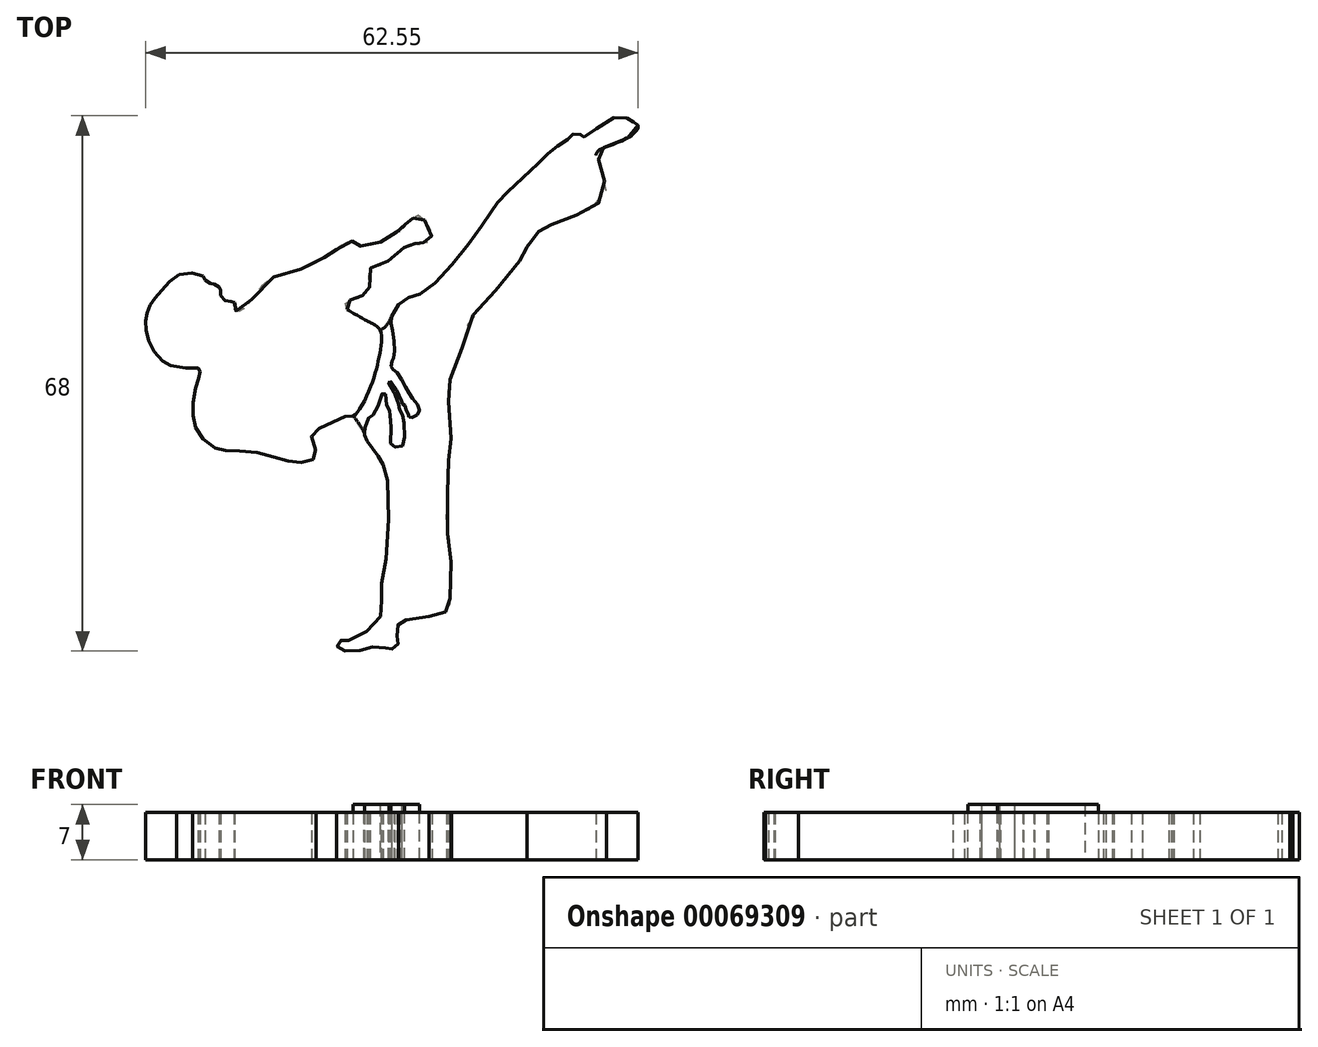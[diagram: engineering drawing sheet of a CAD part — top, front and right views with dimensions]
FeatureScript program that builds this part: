
annotation { "Feature Type Name" : "Feature", "Feature Type Description" : "" }
export const myFeature = defineFeature(function(context is Context, id is Id, definition is map)
    precondition{}
    {
        {
            var Q0;
            Q0=qCreatedBy(makeId("Top.planeOp"),FACE);
            var sketch = newSketch(context, id + "F0", { "sketchPlane" : qUnion([Q0])});
            skFitSpline(sketch, "E0", {"points": [v(-51.75, 44.73) * mm, v(-51.95, 44.9) * mm, v(-52.69, 44.87) * mm, v(-53.47, 45.56) * mm, v(-53.55, 46.35) * mm, v(-53.7, 46.52) * mm, v(-53.72, 46.74) * mm, v(-54.43, 47.11) * mm, v(-54.6, 47.11) * mm, v(-55.44, 47.53) * mm, v(-55.52, 47.92) * mm, v(-58.15, 48.5) * mm, v(-60.84, 46.52) * mm, v(-62.26, 44.78) * mm, v(-62.91, 43.3) * mm, v(-63.01, 41.6) * mm, v(-62.19, 38.9) * mm, v(-60.02, 36.77) * mm, v(-59.1, 36.6) * mm], "startDerivative": vector(-5.65, 8.4) * mm, "endDerivative": vector(13.6, -5.83) * mm});
            skFitSpline(sketch, "E1", {"points": [v(-59.1, 36.6) * mm, v(-58.93, 36.45) * mm, v(-56.37, 36.43) * mm, v(-56.37, 36.3) * mm, v(-56.18, 36.2) * mm, v(-56.26, 35.4) * mm, v(-56.34, 34.96) * mm, v(-56.97, 32.75) * mm, v(-56.97, 30.15) * mm, v(-56.33, 28.15) * mm, v(-53.97, 26.16) * mm, v(-52.28, 25.94) * mm, v(-48.26, 25.57) * mm, v(-44.9, 24.58) * mm, v(-42.47, 24.58) * mm, v(-41.39, 25.43) * mm, v(-41.98, 27.9) * mm, v(-40.1, 29.11) * mm, v(-37.6, 30.32) * mm, v(-36.68, 30.34) * mm, v(-34.38, 34.29) * mm, v(-33.24, 38.67) * mm, v(-33.27, 41.23) * mm, v(-34.84, 42.37) * mm, v(-37.44, 43.89) * mm], "startDerivative": vector(3.1, -12.93) * mm, "endDerivative": vector(-51.13, 31.47) * mm});
            skFitSpline(sketch, "E2", {"points": [v(-37.44, 43.89) * mm, v(-37.67, 44.62) * mm, v(-36.78, 45.13) * mm, v(-35.75, 45.43) * mm, v(-35.16, 46) * mm, v(-34.62, 46.46) * mm, v(-34.62, 49) * mm, v(-33.44, 49.34) * mm, v(-30.65, 51.38) * mm, v(-29.88, 51.98) * mm, v(-29.12, 52.24) * mm, v(-28.12, 52.22) * mm, v(-27.96, 52.4) * mm, v(-27.47, 52.36) * mm, v(-26.84, 52.87) * mm, v(-26.75, 53.72) * mm, v(-28.1, 55.68) * mm, v(-28.84, 55.7) * mm, v(-29.42, 55.05) * mm, v(-29.7, 55) * mm, v(-30.7, 53.95) * mm, v(-31.07, 53.82) * mm, v(-31.57, 53.33) * mm, v(-34.55, 52.02) * mm, v(-36.05, 52.02) * mm, v(-36.45, 52.4) * mm, v(-37.2, 52.5) * mm, v(-38.92, 51.4) * mm, v(-39.89, 50.8) * mm, v(-42.93, 49.1) * mm, v(-47.62, 47.46) * mm, v(-51.02, 43.62) * mm, v(-51.75, 43.89) * mm, v(-51.75, 44.36) * mm, v(-51.75, 44.73) * mm], "startDerivative": vector(-19.72, 33.34) * mm, "endDerivative": vector(-1.61, 21.78) * mm});
            skFitSpline(sketch, "E3", {"points": [v(-0.5, 67.29) * mm, v(-0.95, 67.65) * mm, v(-1.34, 67.68) * mm, v(-2.74, 68.47) * mm, v(-7.15, 65.88) * mm, v(-7.63, 65.81) * mm, v(-7.81, 66.14) * mm, v(-8.73, 66.17) * mm, v(-9.37, 65.51) * mm, v(-11.24, 64.27) * mm, v(-13.23, 62.38) * mm, v(-17.7, 58.2) * mm, v(-19, 56.5) * mm, v(-22.44, 51.68) * mm, v(-28.21, 45.8) * mm, v(-30.08, 45.22) * mm, v(-31.8, 42.95) * mm, v(-31.64, 41.03) * mm, v(-31.52, 37.76) * mm, v(-31.73, 37.35) * mm, v(-31.8, 36.44) * mm, v(-31.33, 36.1) * mm, v(-30.08, 34.08) * mm, v(-29.16, 32.6) * mm, v(-28.26, 31.1) * mm, v(-28.89, 30.26) * mm, v(-29.51, 30.14) * mm, v(-29.66, 30.5) * mm, v(-29.97, 31) * mm, v(-30.15, 31.7) * mm, v(-30.44, 31.9) * mm, v(-30.55, 32.26) * mm], "startDerivative": vector(-22.63, 25.11) * mm, "endDerivative": vector(0.32, 27.82) * mm});
            skFitSpline(sketch, "E4", {"points": [v(-30.55, 32.26) * mm, v(-31.41, 34.1) * mm, v(-32.04, 34.78) * mm, v(-32.22, 34.7) * mm, v(-31.83, 34.04) * mm, v(-30.88, 31.76) * mm, v(-30.8, 31.52) * mm, v(-30.76, 30.88) * mm, v(-30.37, 30.4) * mm, v(-30.24, 29.22) * mm, v(-30.24, 26.75) * mm, v(-30.72, 26.45) * mm, v(-31.65, 26.42) * mm, v(-31.94, 26.9) * mm, v(-31.91, 30.32) * mm, v(-32.12, 30.44) * mm, v(-32.1, 31.06) * mm, v(-32.4, 31.45) * mm, v(-32.58, 33.04) * mm, v(-32.87, 33.42) * mm, v(-33.4, 31.9) * mm, v(-34.21, 30.46) * mm, v(-34.5, 30.43) * mm, v(-35.09, 29.13) * mm, v(-35.23, 28.5) * mm, v(-35.22, 27.93) * mm, v(-34.86, 27.59) * mm, v(-34.92, 27.02) * mm, v(-32.92, 24.42) * mm, v(-32.94, 24.2) * mm, v(-32.7, 23.97) * mm, v(-32.42, 12.7) * mm, v(-33.17, 7.74) * mm, v(-33.04, 5.3) * mm, v(-35.67, 2.54) * mm, v(-37.86, 1.7) * mm, v(-38.07, 1.81) * mm, v(-38.7, 1.7) * mm, v(-38.66, 0.94) * mm, v(-38.18, 0.6) * mm, v(-36.09, 0.52) * mm, v(-34.84, 0.87) * mm, v(-32.75, 0.98) * mm, v(-32.44, 0.73) * mm, v(-31.8, 0.69) * mm, v(-31.6, 0.83) * mm, v(-31, 1.3) * mm, v(-31, 2.28) * mm, v(-31.1, 2.45) * mm, v(-31.04, 3.62) * mm, v(-30.64, 4.29) * mm, v(-27.05, 4.84) * mm], "startDerivative": vector(-31.67, 76.04) * mm, "endDerivative": vector(175.6, 37.73) * mm});
            skFitSpline(sketch, "E5", {"points": [v(-27.05, 4.84) * mm, v(-25.77, 5.25) * mm, v(-25.16, 5.32) * mm, v(-24.3, 6) * mm, v(-24.32, 6.21) * mm, v(-24.38, 8.42) * mm, v(-24.29, 13.42) * mm, v(-24.78, 15.79) * mm, v(-24.64, 21.91) * mm, v(-24.52, 24.82) * mm, v(-24.21, 25.82) * mm, v(-24.52, 29.66) * mm, v(-24.56, 33.48) * mm, v(-24.44, 34.73) * mm, v(-23.22, 37.75) * mm, v(-21.83, 42.48) * mm, v(-19.95, 44.8) * mm, v(-16.18, 49.14) * mm, v(-14.87, 51.03) * mm, v(-14.63, 51.43) * mm, v(-14.6, 51.96) * mm, v(-13.45, 53.54) * mm, v(-13.1, 53.79) * mm, v(-12.4, 54.31) * mm, v(-11.84, 54.53) * mm, v(-9.26, 55.6) * mm, v(-7.74, 56.04) * mm, v(-5.59, 57.29) * mm, v(-4.54, 59.32) * mm, v(-5.08, 60.96) * mm, v(-5.43, 62.8) * mm, v(-5.82, 63.41) * mm, v(-5.55, 64.05) * mm, v(-3.65, 64.85) * mm, v(-1.56, 65.86) * mm, v(-0.55, 66.79) * mm, v(-0.5, 67.29) * mm], "startDerivative": vector(60.81, 23.15) * mm, "endDerivative": vector(-3.75, 33.4) * mm});
            skFitSpline(sketch, "E6", {"points": [v(-36.68, 30.34) * mm, v(-35.55, 28.72) * mm, v(-35.22, 27.93) * mm], "startDerivative": vector(2.18, -2.9) * mm, "endDerivative": vector(0.64, -1.86) * mm});
            skFitSpline(sketch, "E7", {"points": [v(-33.27, 41.23) * mm, v(-32.58, 41.72) * mm, v(-31.8, 42.95) * mm], "startDerivative": vector(1.63, 0.9) * mm, "endDerivative": vector(1.31, 2.47) * mm});
            skSolve(sketch);
        }
        {
            var Q0;
            {var subQ3=sQuery(id+"F0.wireOp",EDGE,"E0");Q0=makeQuery(id+"F0.imprint","IMPRINT",FACE,{"disambiguationData":[TD([[makeQuery(id+"F0.imprint","IMPRINT",EDGE,{"derivedFrom":subQ3}),1.0]])]});}
            var Q1;
            {var subQ0=sQuery(id+"F0.wireOp",EDGE,"E5");Q1=makeQuery(id+"F0.imprint","IMPRINT",FACE,{"disambiguationData":[TD([[makeQuery(id+"F0.imprint","IMPRINT",EDGE,{"derivedFrom":subQ0}),1.0]])]});}
            extrude(context, id + "F1", {"entities" : qUnion([Q0, Q1]), "depth" : 6 * mm});
        }
        {
            var Q0;
            {var subQ7=sQuery(id+"F0.wireOp",EDGE,"E7");Q0=makeQuery(id+"F0.imprint","IMPRINT",FACE,{"disambiguationData":[TD([[makeQuery(id+"F0.imprint","IMPRINT",EDGE,{"derivedFrom":subQ7}),-1.0]])]});}
            extrude(context, id + "F2", {"entities" : qUnion([Q0]), "depth" : 7 * mm});
        }
    });
